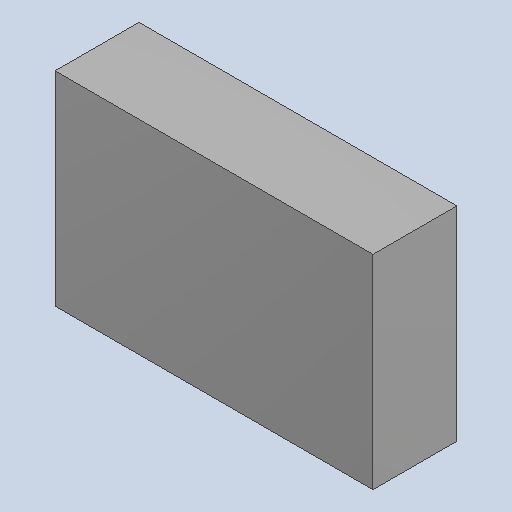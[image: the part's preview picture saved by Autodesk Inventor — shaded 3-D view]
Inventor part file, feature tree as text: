
AUTODESK INVENTOR PART (.ipt)
format: ipt  version: 2023.4 (Build 274418000, 418)  size: 82,944 bytes
history: native  units: mm
features: extrude x1
ambient origin geometry x8: Origin, YZ Plane, XZ Plane, XY Plane, X Axis, Y Axis, Z Axis, Center Point
bodies: Solid1 (feature_tree)
feature tree (1):
  extrude  "Extruded_2"  [1 undecoded]
note: 1 required parameter value undecoded (feature->parameter linkage not recoverable at this tier; creation-order binding heuristic only, values carry confidence <= 0.55)
